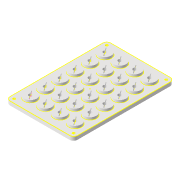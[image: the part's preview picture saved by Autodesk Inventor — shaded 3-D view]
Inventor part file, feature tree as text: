
AUTODESK INVENTOR PART (.ipt)
format: ipt  version: 2022 (Build 260153000, 153)  size: 606,720 bytes
history: native  units: mm
features: projected_geometry x17, sketch x7, extrude x4, hole x2, fillet x1, pattern_linear x1
ambient origin geometry x8: Origin, YZ Plane, XZ Plane, XY Plane, X Axis, Y Axis, Z Axis, Center Point
bodies: Volumenkörper1 (feature_tree)
feature tree (32):
  extrude  "Extrusion1"  Depth=127.5mm
  extrude  "Extrusion2"  Depth=5.0mm
  fillet  "Rundung1"  Radius=16.5mm
  hole  "Bohrung1"  [1 undecoded]
  extrude  "Extrusion3"  Depth=0.85mm
  pattern_linear  "Rechteckige Anordnung2"  Spacing1=0.85mm  [1 undecoded]
  extrude  "Extrusion4"  Depth=6.0mm TaperAngle=0.0deg
  hole  "Bohrung2"  [1 undecoded]
  sketch  "Skizze7"  dims[d25=13.2mm d26=0.85mm d27=6.0mm d28=0.0mm d29=60.0mm d31=18.9mm d32=40.0mm d34=18.9mm d35=13.2mm d36=21.816616mm d37=0.85mm d38=2.0mm d39=0.0mm d40=2.8mm d41=6.0mm d42=4.0mm d43=2.0mm d44=90.0deg d45=8.0mm d46=20.594885mm d30=0.375mm d33=20.594885mm]
  sketch  "Skizze1"  dims[d0=85.5mm d1=127.5mm]
  sketch  "Skizze2"  dims[d2=5.0mm d3=0.0mm d4=16.0mm d5=16.5mm]
  projected_geometry  "Projizierte Kontur1"
  sketch  "Skizze3"  dims[d6=14.4mm d7=3.0mm d8=0.0mm]
  projected_geometry  "Projizierte Kontur2"
  projected_geometry  "Projizierte Kontur3"
  sketch  "Skizze4"  dims[d15=0.85mm d16=13.0mm]
  projected_geometry  "Projizierte Kontur4"
  sketch  "Skizze5"  dims[d17=5.0mm]
  projected_geometry  "Projizierte Kontur5"
  sketch  "Skizze6"  dims[d18=4.6mm d19=6.0mm d20=4.0mm d21=2.0mm d22=90.0deg d23=0.01mm d24=20.594885mm]
  projected_geometry  "Projizierte Kontur6"
  projected_geometry  "Projizierte Kontur7"
  projected_geometry  "Projizierte Kontur8"
  projected_geometry  "Projizierte Kontur9"
  projected_geometry  "Projizierte Kontur10"
  projected_geometry  "Projizierte Kontur11"
  projected_geometry  "Projizierte Kontur12"
  projected_geometry  "Projizierte Kontur13"
  projected_geometry  "Projizierte Kontur14"
  projected_geometry  "Projizierte Kontur15"
  projected_geometry  "Projizierte Kontur16"
  projected_geometry  "Projizierte Kontur17"
note: 3 required parameter values undecoded (feature->parameter linkage not recoverable at this tier; creation-order binding heuristic only, values carry confidence <= 0.55)
